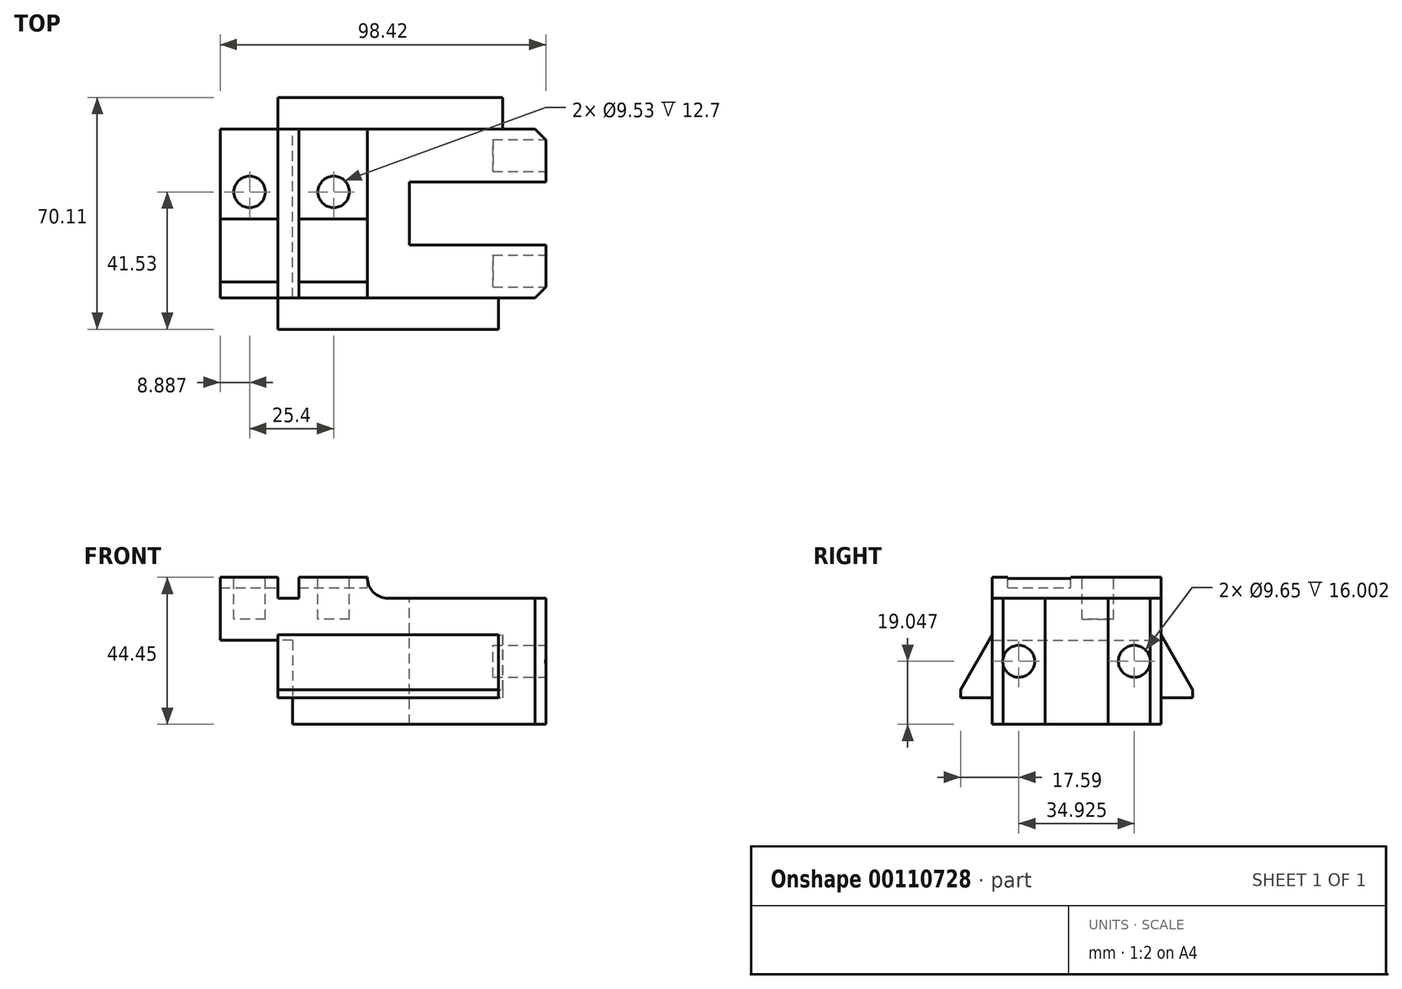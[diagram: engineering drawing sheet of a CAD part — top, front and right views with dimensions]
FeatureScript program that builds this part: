
annotation { "Feature Type Name" : "Feature", "Feature Type Description" : "" }
export const myFeature = defineFeature(function(context is Context, id is Id, definition is map)
    precondition{}
    {
        {
            var Q0;
            Q0=qCreatedBy(makeId("Front.planeOp"),FACE);
            var sketch = newSketch(context, id + "F0", { "sketchPlane" : qUnion([Q0])});
            skLineSegment(sketch, "E0", {"start": v(-16.92, 8.79) * mm, "end": v(-16.92, -16.61) * mm});
            skLineSegment(sketch, "E1", {"start": v(-16.92, 8.79) * mm, "end": v(-38.78, 8.79) * mm});
            skLineSegment(sketch, "E2", {"start": v(-38.78, 8.79) * mm, "end": v(-38.78, 27.84) * mm});
            skLineSegment(sketch, "E3", {"start": v(-16.92, -16.61) * mm, "end": v(59.64, -16.61) * mm});
            skLineSegment(sketch, "E4", {"start": v(-38.78, 27.84) * mm, "end": v(-21.32, 27.84) * mm});
            skLineSegment(sketch, "E5", {"start": v(-21.32, 27.84) * mm, "end": v(-21.32, 21.49) * mm});
            skLineSegment(sketch, "E6", {"start": v(-21.32, 21.49) * mm, "end": v(-15.05, 21.49) * mm});
            skLineSegment(sketch, "E7", {"start": v(-15.05, 21.49) * mm, "end": v(-15.05, 27.84) * mm});
            skLineSegment(sketch, "E8", {"start": v(-15.05, 27.84) * mm, "end": v(5.65, 27.84) * mm});
            skLineSegment(sketch, "E9", {"start": v(5.65, 27.84) * mm, "end": v(5.65, 21.49) * mm});
            skLineSegment(sketch, "E10", {"start": v(5.65, 21.49) * mm, "end": v(59.64, 21.49) * mm});
            skLineSegment(sketch, "E11", {"start": v(59.64, 21.49) * mm, "end": v(59.64, -16.61) * mm});
            skSolve(sketch);
        }
        {
            var Q0;
            Q0 = qSketchRegion(id + "F0", true);
            extrude(context, id + "F1", {"entities" : qUnion([Q0]), "depth" : 51.05 * mm});
        }
        {
            var Q0;
            Q0=makeQuery(id+"F1.opExtrude","SWEPT_EDGE",EDGE,{"disambiguationData":[OSD([sQuery(id+"F0.wireOp",EDGE,"E9"),sQuery(id+"F0.wireOp",EDGE,"E10")])]});
            fillet(context, id + "F2", {"entities" : qUnion([Q0]), "radius" : 6.35 * mm, "tangentPropagation" : true, "allowEdgeOverflow" : false});
        }
        {
            var Q0;
            Q0=makeQuery(id+"F1.opExtrude","SWEPT_FACE",FACE,{"disambiguationData":[OSD([sQuery(id+"F0.wireOp",EDGE,"E10")])]});
            var sketch = newSketch(context, id + "F3", { "sketchPlane" : qUnion([Q0])});
            skLineSegment(sketch, "E12.bottom", {"start": v(59.64, -35.05) * mm, "end": v(18.37, -35.05) * mm});
            skLineSegment(sketch, "E12.top", {"start": v(59.64, -16) * mm, "end": v(18.37, -16) * mm});
            skLineSegment(sketch, "E12.left", {"start": v(59.64, -35.05) * mm, "end": v(59.64, -16) * mm});
            skLineSegment(sketch, "E12.right", {"start": v(18.37, -35.05) * mm, "end": v(18.37, -16) * mm});
            skSolve(sketch);
        }
        {
            var Q0;
            Q0 = qSketchRegion(id + "F3", true);
            extrude(context, id + "F4", {"entities" : qUnion([Q0]), "operationType" : NewBodyOperationType.REMOVE, "oppositeDirection" : true, "depth" : 76.2 * mm});
        }
        {
            var Q0;
            Q0=makeQuery(id+"F1.opExtrude","CAP_EDGE",EDGE,{"disambiguationData":[OSD([sQuery(id+"F0.wireOp",EDGE,"E11")])],"isStart":false});
            var Q1;
            Q1=makeQuery(id+"F1.opExtrude","CAP_EDGE",EDGE,{"disambiguationData":[OSD([sQuery(id+"F0.wireOp",EDGE,"E11")])],"isStart":true});
            chamfer(context, id + "F5", {"entities" : qUnion([Q0, Q1]), "chamferType" : ChamferType.OFFSET_ANGLE, "width" : 3.3 * mm, "oppositeDirection" : false, "angle" : 45 * degree, "tangentPropagation" : true});
        }
        {
            var Q0;
            Q0=makeQuery(id+"F1.opExtrude","SWEPT_FACE",FACE,{"disambiguationData":[OSD([sQuery(id+"F0.wireOp",EDGE,"E4")])]});
            var sketch = newSketch(context, id + "F6", { "sketchPlane" : qUnion([Q0])});
            skLineSegment(sketch, "E13.bottom", {"start": v(-38.78, -27.24) * mm, "end": v(5.67, -27.24) * mm});
            skLineSegment(sketch, "E13.top", {"start": v(-38.78, -46.3) * mm, "end": v(5.67, -46.3) * mm});
            skLineSegment(sketch, "E13.left", {"start": v(-38.78, -27.24) * mm, "end": v(-38.78, -46.3) * mm});
            skLineSegment(sketch, "E13.right", {"start": v(5.67, -27.24) * mm, "end": v(5.67, -46.3) * mm});
            skSolve(sketch);
        }
        {
            var Q0;
            Q0 = qSketchRegion(id + "F6", true);
            extrude(context, id + "F7", {"entities" : qUnion([Q0]), "operationType" : NewBodyOperationType.REMOVE, "oppositeDirection" : true, "depth" : 3.17 * mm});
        }
        {
            var Q0;
            {var subQ0=sQuery(id+"F0.wireOp",EDGE,"E11");Q0=makeQuery(id+"F4.boolean.opBoolean","SPLIT",FACE,{"disambiguationData":[TD([makeQuery(id+"F4.opExtrude","SWEPT_FACE",FACE,{"disambiguationData":[OSD([sQuery(id+"F3.wireOp",EDGE,"E12.bottom")])]})])],"derivedFrom":makeQuery(id+"F1.opExtrude","SWEPT_FACE",FACE,{"disambiguationData":[OSD([subQ0])]})});}
            var sketch = newSketch(context, id + "F8", { "sketchPlane" : qUnion([Q0])});
            skCircle(sketch, "E14", {"center": v(-42.99, 2.44) * mm, "radius": 4.83 * mm});
            skCircle(sketch, "E15", {"center": v(-8.06, 2.44) * mm, "radius": 4.83 * mm});
            skSolve(sketch);
        }
        {
            var Q0;
            Q0 = qSketchRegion(id + "F8", true);
            extrude(context, id + "F9", {"entities" : qUnion([Q0]), "operationType" : NewBodyOperationType.REMOVE, "oppositeDirection" : true, "depth" : 16 * mm});
        }
        {
            var Q0;
            {var subQ2=sQuery(id+"F0.wireOp",EDGE,"E8");Q0=makeQuery(id+"F7.boolean.opBoolean","SPLIT",FACE,{"disambiguationData":[TD([makeQuery(id+"F7.opExtrude","SWEPT_FACE",FACE,{"disambiguationData":[OSD([sQuery(id+"F6.wireOp",EDGE,"E13.bottom")])]})])],"derivedFrom":makeQuery(id+"F1.opExtrude","SWEPT_FACE",FACE,{"disambiguationData":[OSD([subQ2])]})});}
            var sketch = newSketch(context, id + "F10", { "sketchPlane" : qUnion([Q0])});
            skCircle(sketch, "E16", {"center": v(-29.9, -19.05) * mm, "radius": 4.76 * mm});
            skCircle(sketch, "E17", {"center": v(-4.5, -19.05) * mm, "radius": 4.76 * mm});
            skSolve(sketch);
        }
        {
            var Q0;
            Q0 = qSketchRegion(id + "F10", true);
            extrude(context, id + "F11", {"entities" : qUnion([Q0]), "operationType" : NewBodyOperationType.REMOVE, "oppositeDirection" : true, "depth" : 12.7 * mm});
        }
        {
            var Q0;
            Q0=makeQuery(id+"F1.opExtrude","CAP_FACE",FACE,{"disambiguationData":[OSD([sQuery(id+"F0.wireOp",EDGE,"E0"),sQuery(id+"F0.wireOp",EDGE,"E1"),sQuery(id+"F0.wireOp",EDGE,"E2"),sQuery(id+"F0.wireOp",EDGE,"E3"),sQuery(id+"F0.wireOp",EDGE,"E4"),sQuery(id+"F0.wireOp",EDGE,"E5"),sQuery(id+"F0.wireOp",EDGE,"E6"),sQuery(id+"F0.wireOp",EDGE,"E7"),sQuery(id+"F0.wireOp",EDGE,"E8"),sQuery(id+"F0.wireOp",EDGE,"E9"),sQuery(id+"F0.wireOp",EDGE,"E10"),sQuery(id+"F0.wireOp",EDGE,"E11")])],"isStart":false});
            var sketch = newSketch(context, id + "F12", { "sketchPlane" : qUnion([Q0])});
            skLineSegment(sketch, "E18.bottom", {"start": v(-21.32, 10.44) * mm, "end": v(45.35, 10.44) * mm});
            skLineSegment(sketch, "E18.top", {"start": v(-21.32, -8.61) * mm, "end": v(45.35, -8.61) * mm});
            skLineSegment(sketch, "E18.left", {"start": v(-21.32, 10.44) * mm, "end": v(-21.32, -8.61) * mm});
            skLineSegment(sketch, "E18.right", {"start": v(45.35, 10.44) * mm, "end": v(45.35, -8.61) * mm});
            skSolve(sketch);
        }
        {
            var Q0;
            Q0 = qSketchRegion(id + "F12", true);
            extrude(context, id + "F13", {"entities" : qUnion([Q0]), "operationType" : NewBodyOperationType.ADD, "depth" : 9.52 * mm});
        }
        {
            var Q0;
            Q0=makeQuery(id+"F13.opExtrude","SWEPT_FACE",FACE,{"disambiguationData":[OSD([sQuery(id+"F12.wireOp",EDGE,"E18.right")])]});
            var sketch = newSketch(context, id + "F14", { "sketchPlane" : qUnion([Q0])});
            skLineSegment(sketch, "E19", {"start": v(-51.05, 10.44) * mm, "end": v(-60.58, -6.23) * mm});
            skLineSegment(sketch, "E20", {"start": v(-60.58, -6.23) * mm, "end": v(-60.58, -8.61) * mm});
            skLineSegment(sketch, "E21", {"start": v(-60.58, -6.23) * mm, "end": v(-60.58, 10.44) * mm});
            skLineSegment(sketch, "E22", {"start": v(-60.58, 10.44) * mm, "end": v(-51.05, 10.44) * mm});
            skSolve(sketch);
        }
        {
            var Q0;
            Q0 = qSketchRegion(id + "F14", true);
            extrude(context, id + "F15", {"entities" : qUnion([Q0]), "operationType" : NewBodyOperationType.REMOVE, "oppositeDirection" : true, "depth" : 76.2 * mm});
        }
        {
            var Q0;
            Q0=makeQuery(id+"F1.opExtrude","CAP_FACE",FACE,{"disambiguationData":[OSD([sQuery(id+"F0.wireOp",EDGE,"E0"),sQuery(id+"F0.wireOp",EDGE,"E1"),sQuery(id+"F0.wireOp",EDGE,"E2"),sQuery(id+"F0.wireOp",EDGE,"E3"),sQuery(id+"F0.wireOp",EDGE,"E4"),sQuery(id+"F0.wireOp",EDGE,"E5"),sQuery(id+"F0.wireOp",EDGE,"E6"),sQuery(id+"F0.wireOp",EDGE,"E7"),sQuery(id+"F0.wireOp",EDGE,"E8"),sQuery(id+"F0.wireOp",EDGE,"E9"),sQuery(id+"F0.wireOp",EDGE,"E10"),sQuery(id+"F0.wireOp",EDGE,"E11")])],"isStart":true});
            var sketch = newSketch(context, id + "F16", { "sketchPlane" : qUnion([Q0])});
            skLineSegment(sketch, "E23.bottom", {"start": v(21.32, 10.44) * mm, "end": v(-46.62, 10.44) * mm});
            skLineSegment(sketch, "E23.top", {"start": v(21.32, -8.61) * mm, "end": v(-46.62, -8.61) * mm});
            skLineSegment(sketch, "E23.left", {"start": v(21.32, 10.44) * mm, "end": v(21.32, -8.61) * mm});
            skLineSegment(sketch, "E23.right", {"start": v(-46.62, 10.44) * mm, "end": v(-46.62, -8.61) * mm});
            skSolve(sketch);
        }
        {
            var Q0;
            Q0 = qSketchRegion(id + "F16", true);
            extrude(context, id + "F17", {"entities" : qUnion([Q0]), "operationType" : NewBodyOperationType.ADD, "depth" : 9.52 * mm});
        }
        {
            var Q0;
            Q0=makeQuery(id+"F17.opExtrude","SWEPT_FACE",FACE,{"disambiguationData":[OSD([sQuery(id+"F16.wireOp",EDGE,"E23.right")])]});
            var sketch = newSketch(context, id + "F18", { "sketchPlane" : qUnion([Q0])});
            skLineSegment(sketch, "E24", {"start": v(9.53, -8.61) * mm, "end": v(9.53, -6.23) * mm});
            skLineSegment(sketch, "E25", {"start": v(9.53, -6.23) * mm, "end": v(0, 10.44) * mm});
            skLineSegment(sketch, "E26", {"start": v(9.53, -6.23) * mm, "end": v(9.53, 10.44) * mm});
            skLineSegment(sketch, "E27", {"start": v(9.53, 10.44) * mm, "end": v(0, 10.44) * mm});
            skSolve(sketch);
        }
        {
            var Q0;
            Q0 = qSketchRegion(id + "F18", true);
            extrude(context, id + "F19", {"entities" : qUnion([Q0]), "operationType" : NewBodyOperationType.REMOVE, "endBound" : BoundingType.THROUGH_ALL, "oppositeDirection" : true, "depth" : 25.4 * mm});
        }
    });
